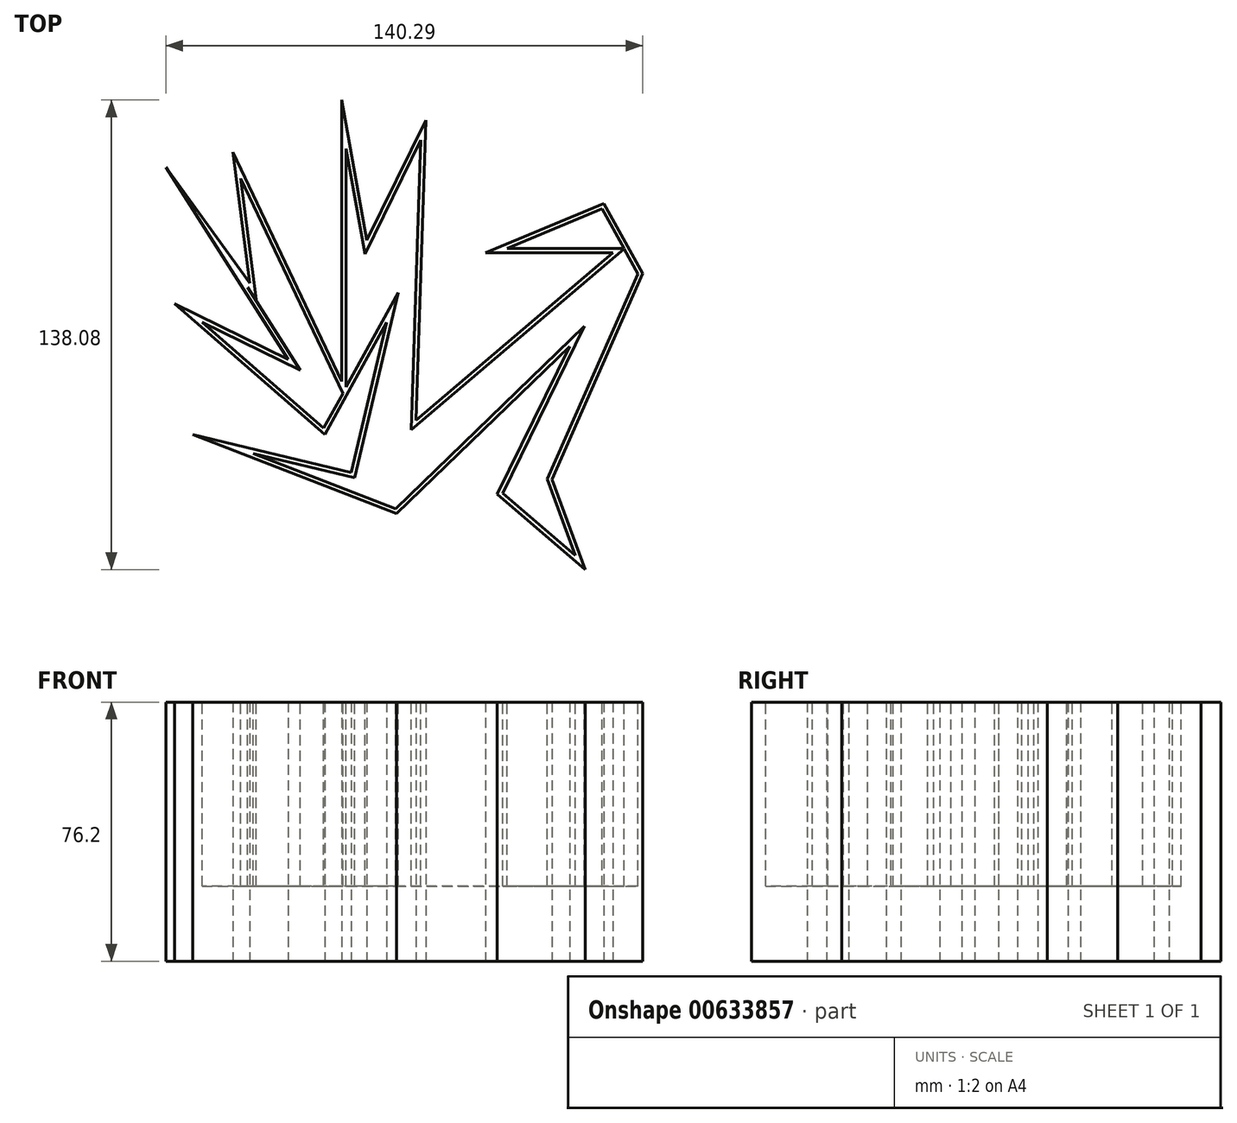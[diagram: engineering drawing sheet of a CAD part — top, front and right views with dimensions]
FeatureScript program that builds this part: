
annotation { "Feature Type Name" : "Feature", "Feature Type Description" : "" }
export const myFeature = defineFeature(function(context is Context, id is Id, definition is map)
    precondition{}
    {
        {
            var Q0;
            Q0=qCreatedBy(makeId("Top.planeOp"),FACE);
            var sketch = newSketch(context, id + "F0", { "sketchPlane" : qUnion([Q0])});
            skLineSegment(sketch, "E0", {"start": v(-43.23, 15.2) * mm, "end": v(-48.2, 53.74) * mm});
            skLineSegment(sketch, "E1", {"start": v(-48.2, 53.74) * mm, "end": v(-16.13, -13.73) * mm});
            skLineSegment(sketch, "E2", {"start": v(-16.13, -13.73) * mm, "end": v(-16.13, 69.04) * mm});
            skLineSegment(sketch, "E3", {"start": v(-16.13, 69.04) * mm, "end": v(-8.76, 27.75) * mm});
            skLineSegment(sketch, "E4", {"start": v(-8.76, 27.75) * mm, "end": v(8.57, 63.14) * mm});
            skLineSegment(sketch, "E5", {"start": v(8.57, 63.14) * mm, "end": v(5.62, -25.16) * mm});
            skLineSegment(sketch, "E6", {"start": v(5.62, -25.16) * mm, "end": v(63.51, 24.06) * mm});
            skLineSegment(sketch, "E7", {"start": v(63.51, 24.06) * mm, "end": v(26.09, 24.06) * mm});
            skLineSegment(sketch, "E8", {"start": v(26.09, 24.06) * mm, "end": v(60.93, 38.62) * mm});
            skLineSegment(sketch, "E9", {"start": v(60.93, 38.62) * mm, "end": v(72.36, 17.97) * mm});
            skLineSegment(sketch, "E10", {"start": v(72.36, 17.97) * mm, "end": v(45.63, -42.5) * mm});
            skLineSegment(sketch, "E11", {"start": v(45.63, -42.5) * mm, "end": v(55.4, -69.04) * mm});
            skLineSegment(sketch, "E12", {"start": v(55.4, -69.04) * mm, "end": v(29.59, -46.92) * mm});
            skLineSegment(sketch, "E13", {"start": v(29.59, -46.92) * mm, "end": v(50.87, -3.45) * mm});
            skLineSegment(sketch, "E14", {"start": v(50.87, -3.45) * mm, "end": v(0, -52.63) * mm});
            skLineSegment(sketch, "E15", {"start": v(0, -52.63) * mm, "end": v(-60, -29.4) * mm});
            skLineSegment(sketch, "E16", {"start": v(-60, -29.4) * mm, "end": v(-13.37, -40.47) * mm});
            skLineSegment(sketch, "E17", {"start": v(-13.37, -40.47) * mm, "end": v(-2.91, 3.62) * mm});
            skLineSegment(sketch, "E18", {"start": v(-2.91, 3.62) * mm, "end": v(-21.1, -29.4) * mm});
            skLineSegment(sketch, "E19", {"start": v(-21.1, -29.4) * mm, "end": v(-65.35, 9.13) * mm});
            skLineSegment(sketch, "E20", {"start": v(-65.35, 9.13) * mm, "end": v(-31.88, -7.26) * mm});
            skLineSegment(sketch, "E21", {"start": v(-31.88, -7.26) * mm, "end": v(-67.93, 49.31) * mm});
            skLineSegment(sketch, "E22", {"start": v(-67.93, 49.31) * mm, "end": v(-43.23, 15.2) * mm});
            skSolve(sketch);
        }
        {
            var Q0;
            Q0=makeQuery(id+"F0.imprint","IMPRINT",FACE,{"disambiguationData":[TD([[makeQuery(id+"F0.imprint","IMPRINT",EDGE,{"derivedFrom":sQuery(id+"F0.wireOp",EDGE,"E0")}),-1.0]])]});
            extrude(context, id + "F1", {"entities" : qUnion([Q0]), "depth" : 76.2 * mm, "offsetDistance" : 25.4 * mm});
        }
        {
            var Q0;
            Q0=makeQuery(id+"F1.opExtrude","CAP_FACE",FACE,{"disambiguationData":[OSD([sQuery(id+"F0.wireOp",EDGE,"E0"),sQuery(id+"F0.wireOp",EDGE,"E1"),sQuery(id+"F0.wireOp",EDGE,"E2"),sQuery(id+"F0.wireOp",EDGE,"E3"),sQuery(id+"F0.wireOp",EDGE,"E4"),sQuery(id+"F0.wireOp",EDGE,"E5"),sQuery(id+"F0.wireOp",EDGE,"E6"),sQuery(id+"F0.wireOp",EDGE,"E7"),sQuery(id+"F0.wireOp",EDGE,"E8"),sQuery(id+"F0.wireOp",EDGE,"E9"),sQuery(id+"F0.wireOp",EDGE,"E10"),sQuery(id+"F0.wireOp",EDGE,"E11"),sQuery(id+"F0.wireOp",EDGE,"E12"),sQuery(id+"F0.wireOp",EDGE,"E13"),sQuery(id+"F0.wireOp",EDGE,"E14"),sQuery(id+"F0.wireOp",EDGE,"E15"),sQuery(id+"F0.wireOp",EDGE,"E16"),sQuery(id+"F0.wireOp",EDGE,"E17"),sQuery(id+"F0.wireOp",EDGE,"E18"),sQuery(id+"F0.wireOp",EDGE,"E19"),sQuery(id+"F0.wireOp",EDGE,"E20"),sQuery(id+"F0.wireOp",EDGE,"E21"),sQuery(id+"F0.wireOp",EDGE,"E22")])],"isStart":false});
            var sketch = newSketch(context, id + "F2", { "sketchPlane" : qUnion([Q0])});
            skLineSegment(sketch, "E23.0", {"start": v(32.42, 25.33) * mm, "end": v(66.84, 25.33) * mm});
            skLineSegment(sketch, "E23.1", {"start": v(60.37, 37.01) * mm, "end": v(32.42, 25.33) * mm});
            skLineSegment(sketch, "E23.2", {"start": v(66.84, 25.33) * mm, "end": v(60.37, 37.01) * mm});
            skLineSegment(sketch, "E23.3", {"start": v(-43.91, 13.98) * mm, "end": v(-28.38, -10.4) * mm});
            skLineSegment(sketch, "E23.4", {"start": v(-41.33, 10.42) * mm, "end": v(-43.91, 13.98) * mm});
            skLineSegment(sketch, "E23.5", {"start": v(-14.86, -15.44) * mm, "end": v(0.48, 12.4) * mm});
            skLineSegment(sketch, "E23.6", {"start": v(-28.38, -10.4) * mm, "end": v(-57.23, 3.73) * mm});
            skLineSegment(sketch, "E23.7", {"start": v(0.48, 12.4) * mm, "end": v(-12.42, -42) * mm});
            skLineSegment(sketch, "E23.8", {"start": v(-57.23, 3.73) * mm, "end": v(-21.46, -27.41) * mm});
            skLineSegment(sketch, "E23.9", {"start": v(-15.86, -17.26) * mm, "end": v(-45.93, 45.98) * mm});
            skLineSegment(sketch, "E23.10", {"start": v(-42.22, -34.93) * mm, "end": v(-0.3, -51.16) * mm});
            skLineSegment(sketch, "E23.11", {"start": v(-45.93, 45.98) * mm, "end": v(-41.33, 10.42) * mm});
            skLineSegment(sketch, "E23.12", {"start": v(-0.3, -51.16) * mm, "end": v(55.2, 2.5) * mm});
            skLineSegment(sketch, "E23.13", {"start": v(55.2, 2.5) * mm, "end": v(31.16, -46.6) * mm});
            skLineSegment(sketch, "E23.14", {"start": v(31.16, -46.6) * mm, "end": v(52.52, -64.9) * mm});
            skLineSegment(sketch, "E23.15", {"start": v(52.52, -64.9) * mm, "end": v(44.26, -42.45) * mm});
            skLineSegment(sketch, "E23.16", {"start": v(44.26, -42.45) * mm, "end": v(70.94, 17.91) * mm});
            skLineSegment(sketch, "E23.17", {"start": v(-12.42, -42) * mm, "end": v(-42.22, -34.93) * mm});
            skLineSegment(sketch, "E23.18", {"start": v(-21.46, -27.41) * mm, "end": v(-15.86, -17.26) * mm});
            skLineSegment(sketch, "E23.19", {"start": v(-14.86, 54.7) * mm, "end": v(-14.86, -15.44) * mm});
            skLineSegment(sketch, "E23.20", {"start": v(70.94, 17.91) * mm, "end": v(66.88, 25.25) * mm});
            skLineSegment(sketch, "E23.21", {"start": v(66.88, 25.25) * mm, "end": v(4.26, -28) * mm});
            skLineSegment(sketch, "E23.22", {"start": v(4.26, -28) * mm, "end": v(7.1, 57.26) * mm});
            skLineSegment(sketch, "E23.23", {"start": v(7.1, 57.26) * mm, "end": v(-9.32, 23.7) * mm});
            skLineSegment(sketch, "E23.24", {"start": v(-9.32, 23.7) * mm, "end": v(-14.86, 54.7) * mm});
            skSolve(sketch);
        }
        {
            var Q0;
            Q0=makeQuery(id+"F2.imprint","IMPRINT",FACE,{"disambiguationData":[TD([[makeQuery(id+"F2.imprint","IMPRINT",EDGE,{"derivedFrom":sQuery(id+"F2.wireOp",EDGE,"E23.5")}),1.0]])]});
            var Q1;
            Q1=makeQuery(id+"F2.imprint","IMPRINT",FACE,{"disambiguationData":[TD([[makeQuery(id+"F2.imprint","IMPRINT",EDGE,{"derivedFrom":sQuery(id+"F2.wireOp",EDGE,"E23.0")}),1.0]])]});
            var Q2;
            Q2=makeQuery(id+"F2.imprint","IMPRINT",FACE,{"disambiguationData":[TD([[makeQuery(id+"F2.imprint","IMPRINT",EDGE,{"derivedFrom":sQuery(id+"F2.wireOp",EDGE,"E23.3")}),1.0]])]});
            extrude(context, id + "F3", {"entities" : qUnion([Q0, Q1, Q2]), "operationType" : NewBodyOperationType.REMOVE, "oppositeDirection" : true, "depth" : 54.1 * mm, "offsetDistance" : 25.4 * mm});
        }
    });
